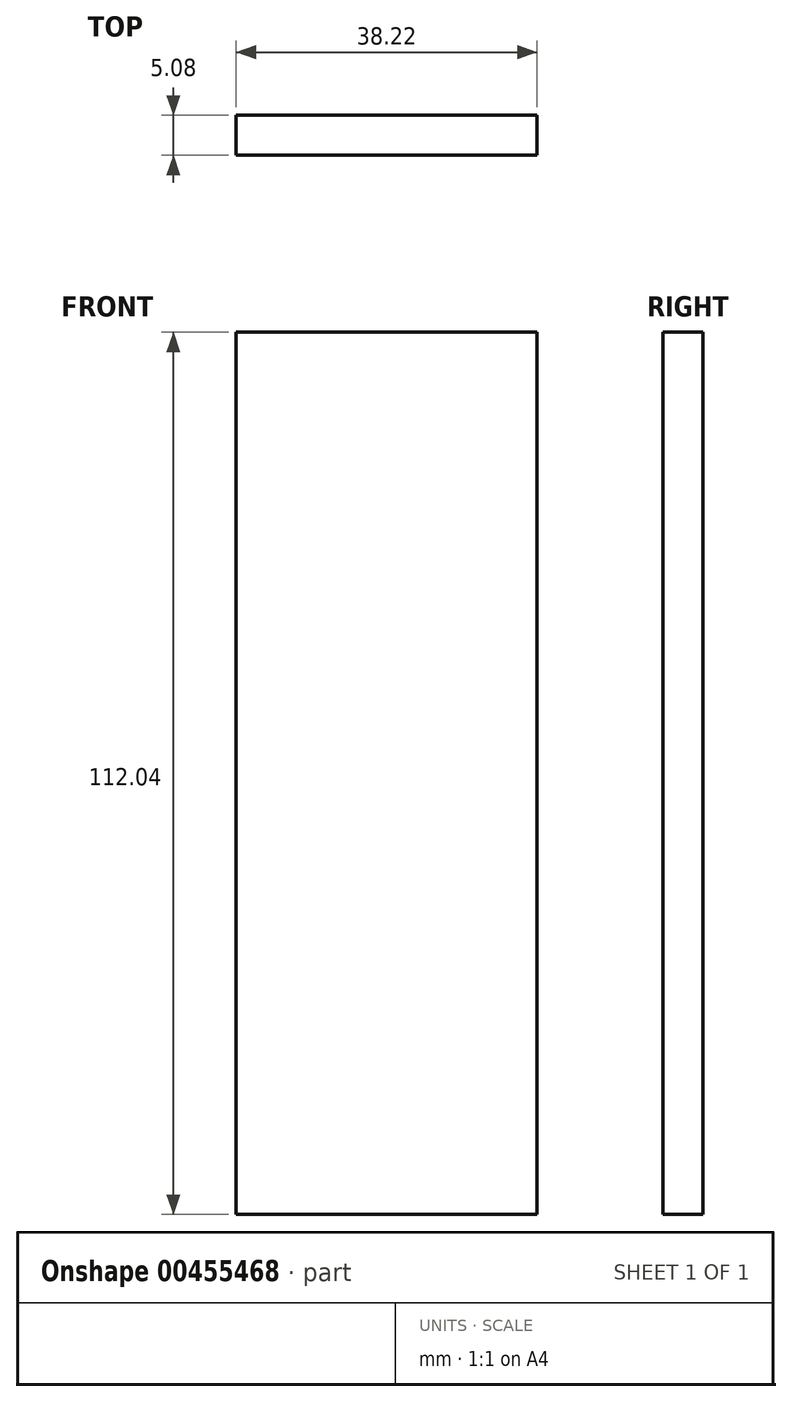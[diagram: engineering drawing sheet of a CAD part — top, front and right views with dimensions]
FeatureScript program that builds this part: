
annotation { "Feature Type Name" : "Feature", "Feature Type Description" : "" }
export const myFeature = defineFeature(function(context is Context, id is Id, definition is map)
    precondition{}
    {
        {
            var Q0;
            Q0=qCreatedBy(makeId("Front.planeOp"),FACE);
            var sketch = newSketch(context, id + "F0", { "sketchPlane" : qUnion([Q0])});
            skLineSegment(sketch, "E0.bottom", {"start": v(-19.77, 56.02) * mm, "end": v(18.45, 56.02) * mm});
            skLineSegment(sketch, "E0.top", {"start": v(-19.77, -56.02) * mm, "end": v(18.45, -56.02) * mm});
            skLineSegment(sketch, "E0.left", {"start": v(-19.77, 56.02) * mm, "end": v(-19.77, -56.02) * mm});
            skLineSegment(sketch, "E0.right", {"start": v(18.45, 56.02) * mm, "end": v(18.45, -56.02) * mm});
            skSolve(sketch);
        }
        {
            var Q0;
            Q0=makeQuery(id+"F0.imprint","IMPRINT",FACE,{"disambiguationData":[TD([[makeQuery(id+"F0.imprint","IMPRINT",EDGE,{"derivedFrom":sQuery(id+"F0.wireOp",EDGE,"E0.bottom")}),-1.0]])]});
            extrude(context, id + "F1", {"entities" : qUnion([Q0]), "depth" : 5.08 * mm});
        }
    });
